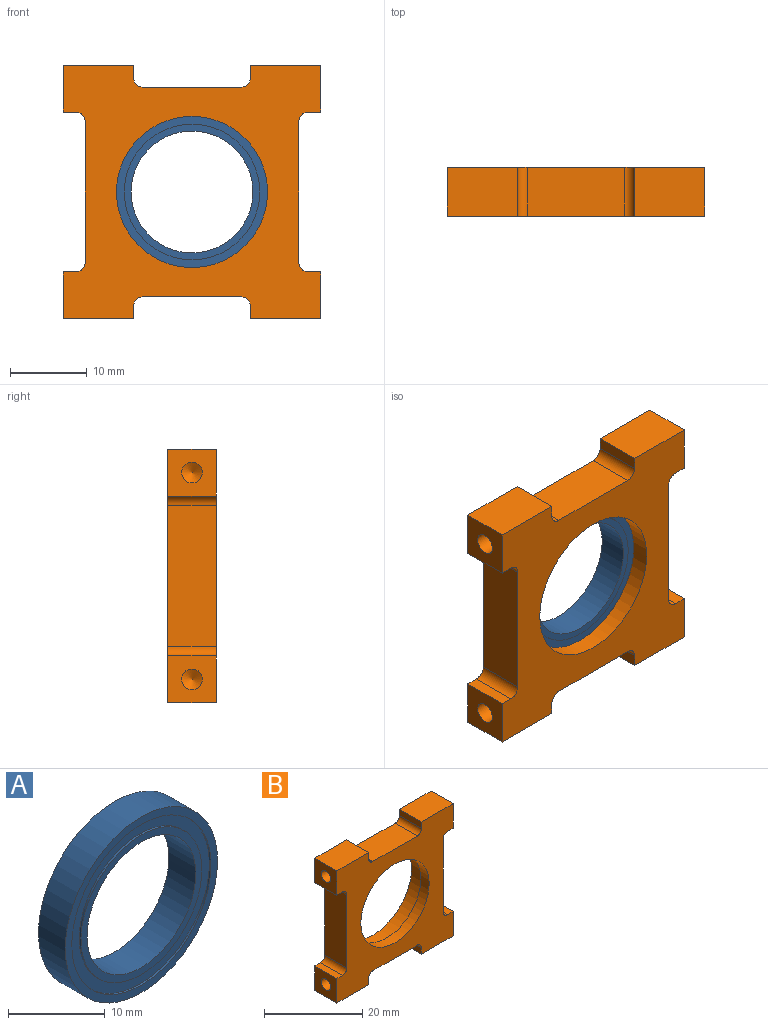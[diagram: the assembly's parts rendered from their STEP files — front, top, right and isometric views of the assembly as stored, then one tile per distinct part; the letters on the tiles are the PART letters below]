
ASSEMBLY  parts=2 mates=1
PART A: 12 faces, bbox 22.2x3.9x22.2 mm
  f0: cylinder r=8.83mm len=17.65mm, axis (0,-1,0), area 14.1mm2, adj f6,f11
  f1: cylinder r=10.16mm len=20.32mm, axis (0,-1,0), area 16.2mm2, adj f9,f11
  f2: cylinder r=8.83mm len=17.65mm, axis (0,1,0), area 14.1mm2, adj f7,f10
  f3: cylinder r=10.16mm len=20.32mm, axis (0,1,0), area 16.2mm2, adj f8,f10
  f4: cylinder r=7.94mm len=15.88mm, axis (0,-1,0), area 195.1mm2, adj f6,f7
  f5: cylinder r=11.11mm len=22.23mm, axis (0,-1,0), area 273.1mm2, adj f8,f9
  f6: plane 17.65x17.65mm, normal (0,-1,0), area 46.8mm2, adj f0,f4
  f7: plane 17.65x17.65mm, normal (0,1,0), area 46.8mm2, adj f2,f4
  f8: plane 22.23x22.23mm, normal (0,1,0), area 63.7mm2, adj f3,f5
  f9: plane 22.23x22.23mm, normal (0,-1,0), area 63.7mm2, adj f1,f5
  f10: plane 20.32x20.32mm, normal (0,1,0), area 79.5mm2, adj f2,f3
  f11: plane 20.32x20.32mm, normal (0,-1,0), area 79.5mm2, adj f0,f1
PART B: 41 faces, bbox 33.5x6.4x33 mm
  f0: cylinder r=9.84mm len=19.69mm, axis (0,1,0), area 147.7mm2, adj f31,f32
  f1: cylinder r=11.11mm len=22.23mm, axis (0,1,0), area 276.7mm2, adj f30,f32
  f2: cylinder r=1.35mm len=7.62mm, axis (1,0,0), area 64.8mm2, adj f3,f26
  f3: cone r=1.35mm half-angle=59deg, axis (1,0,0), area 6.7mm2, adj f2
  f4: cylinder r=1.35mm len=7.62mm, axis (1,0,0), area 64.8mm2, adj f5,f10
  f5: cone r=1.35mm half-angle=59deg, axis (1,0,0), area 6.7mm2, adj f4
  f6: cylinder r=1.35mm len=7.62mm, axis (-1,0,0), area 64.8mm2, adj f7,f20
  f7: cone r=1.35mm half-angle=59deg, axis (-1,0,0), area 6.7mm2, adj f6
  f8: cylinder r=1.35mm len=7.62mm, axis (-1,0,0), area 64.8mm2, adj f9,f16
  f9: cone r=1.35mm half-angle=59deg, axis (-1,0,0), area 6.7mm2, adj f8
  f10: plane 6.35x6.1mm, normal (1,0,0), area 33mm2, adj f4,f11,f29,f30,f31
  f11: plane 9.14x6.35mm, normal (0,0,-1), area 58.1mm2, adj f10,f12,f30,f31
  f12: plane 6.35x1.6mm, normal (-1,0,0), area 10.1mm2, adj f11,f30,f31,f39
  f13: plane 12.7x6.35mm, normal (0,0,-1), area 80.6mm2, adj f30,f31,f38,f39
  f14: plane 6.35x1.6mm, normal (1,0,0), area 10.1mm2, adj f15,f30,f31,f38
  f15: plane 9.14x6.35mm, normal (0,0,-1), area 58.1mm2, adj f14,f16,f30,f31
  f16: plane 6.35x6.1mm, normal (-1,0,0), area 33mm2, adj f8,f15,f17,f30,f31
  f17: plane 6.35x1.59mm, normal (0,0,1), area 10.1mm2, adj f16,f30,f31,f40
  f18: plane 18.29x6.35mm, normal (-1,0,0), area 116.1mm2, adj f30,f31,f37,f40
  f19: plane 6.35x1.59mm, normal (0,0,-1), area 10.1mm2, adj f20,f30,f31,f37
  f20: plane 6.35x6.1mm, normal (-1,0,0), area 33mm2, adj f6,f19,f21,f30,f31
  f21: plane 9.14x6.35mm, normal (0,0,1), area 58.1mm2, adj f20,f22,f30,f31
  f22: plane 6.35x1.6mm, normal (1,0,0), area 10.1mm2, adj f21,f30,f31,f36
  f23: plane 12.7x6.35mm, normal (0,0,1), area 80.6mm2, adj f30,f31,f35,f36
  f24: plane 6.35x1.6mm, normal (-1,0,0), area 10.1mm2, adj f25,f30,f31,f35
  f25: plane 9.14x6.35mm, normal (0,0,1), area 58.1mm2, adj f24,f26,f30,f31
  f26: plane 6.35x6.1mm, normal (1,0,0), area 33mm2, adj f2,f25,f27,f30,f31
  f27: plane 6.35x1.59mm, normal (0,0,-1), area 10.1mm2, adj f26,f30,f31,f34
  f28: plane 18.29x6.35mm, normal (1,0,0), area 116.1mm2, adj f30,f31,f33,f34
  f29: plane 6.35x1.59mm, normal (0,0,1), area 10.1mm2, adj f10,f30,f31,f33
  f30: plane 33.53x33.02mm, normal (0,1,0), area 515.6mm2, adj f1,f10,f11,f12,f13,f14,f15,f16
  f31: plane 33.53x33.02mm, normal (0,-1,0), area 599.2mm2, adj f0,f10,f11,f12,f13,f14,f15,f16
  f32: plane 22.23x22.23mm, normal (0,1,0), area 83.6mm2, adj f0,f1
  f33: cylinder r=1.27mm len=6.35mm, axis (0,1,0), area 12.7mm2, adj f28,f29,f30,f31
  f34: cylinder r=1.27mm len=6.35mm, axis (0,1,0), area 12.7mm2, adj f27,f28,f30,f31
  f35: cylinder r=1.27mm len=6.35mm, axis (0,1,0), area 12.7mm2, adj f23,f24,f30,f31
  f36: cylinder r=1.27mm len=6.35mm, axis (0,1,0), area 12.7mm2, adj f22,f23,f30,f31
  f37: cylinder r=1.27mm len=6.35mm, axis (0,1,0), area 12.7mm2, adj f18,f19,f30,f31
  f38: cylinder r=1.27mm len=6.35mm, axis (0,1,0), area 12.7mm2, adj f13,f14,f30,f31
  f39: cylinder r=1.27mm len=6.35mm, axis (0,1,0), area 12.7mm2, adj f12,f13,f30,f31
  f40: cylinder r=1.27mm len=6.35mm, axis (0,1,0), area 12.7mm2, adj f17,f18,f30,f31
PLACE A rot(axis=(0,-1,0),90deg) t=(9.8,15.87,27.74)mm
PLACE B t=(9.8,13.48,27.74)mm
MATE fastened A.f0 <-> B.f0  axis (0,1,0) through (9.8,15.87,27.74)mm
